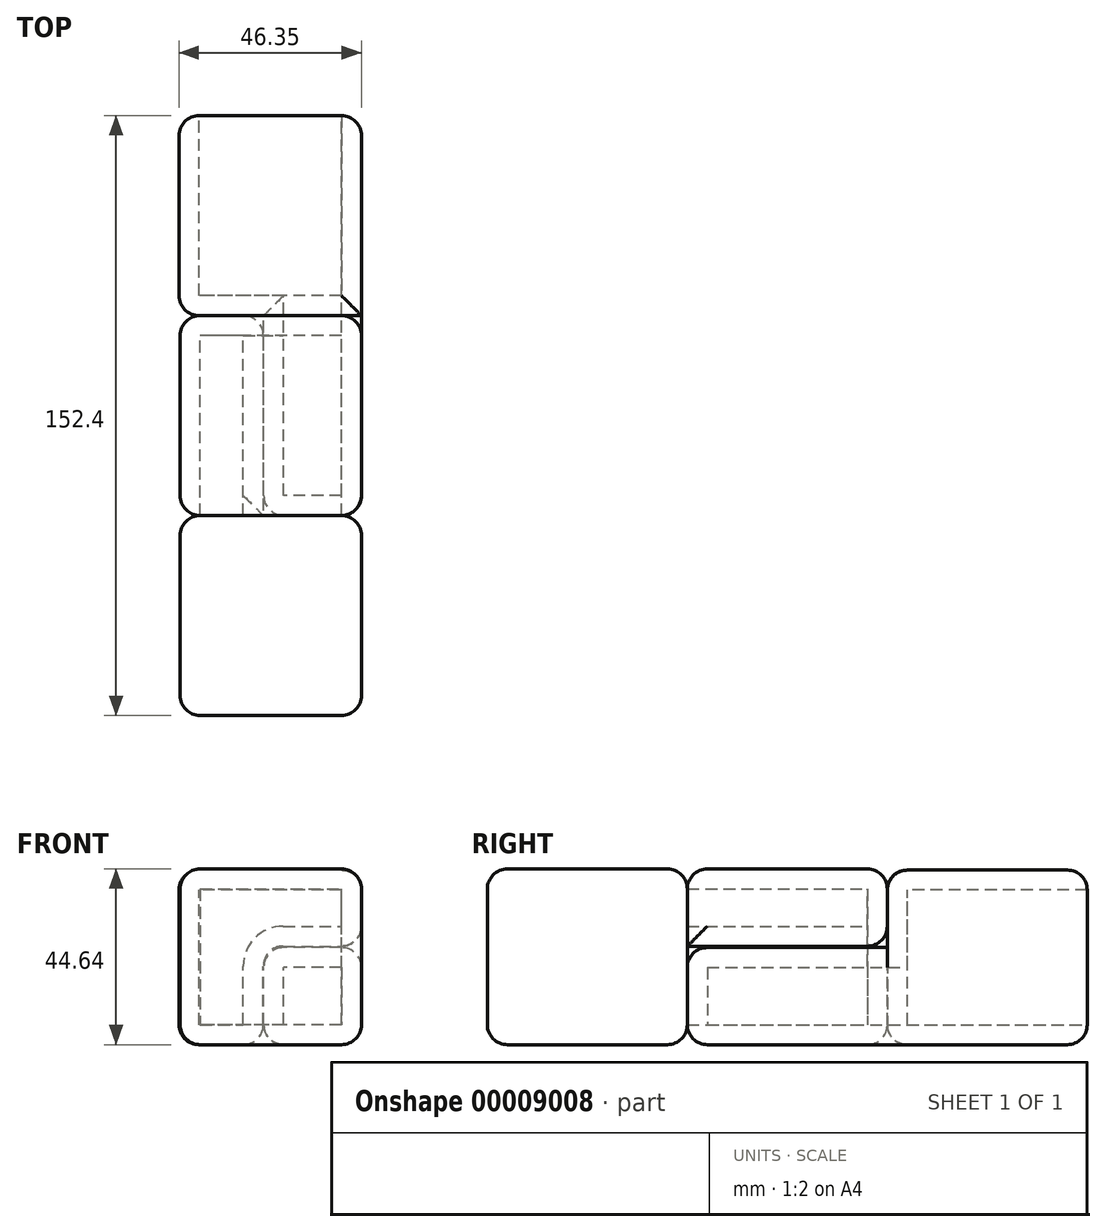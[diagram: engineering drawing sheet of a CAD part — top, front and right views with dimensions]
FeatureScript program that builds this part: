
annotation { "Feature Type Name" : "Feature", "Feature Type Description" : "" }
export const myFeature = defineFeature(function(context is Context, id is Id, definition is map)
    precondition{}
    {
        {
            var Q0;
            Q0=qCreatedBy(makeId("Front.planeOp"),FACE);
            var sketch = newSketch(context, id + "F0", { "sketchPlane" : qUnion([Q0])});
            skLineSegment(sketch, "E0.bottom", {"start": v(0, 0) * mm, "end": v(-46.35, 0) * mm});
            skLineSegment(sketch, "E0.top", {"start": v(0, 44.35) * mm, "end": v(-46.35, 44.35) * mm});
            skLineSegment(sketch, "E0.left", {"start": v(0, 0) * mm, "end": v(0, 44.35) * mm});
            skLineSegment(sketch, "E0.right", {"start": v(-46.35, 0) * mm, "end": v(-46.35, 44.35) * mm});
            skSolve(sketch);
        }
        {
            var Q0;
            Q0=makeQuery(id+"F0.imprint","IMPRINT",FACE,{"disambiguationData":[TD([[makeQuery(id+"F0.imprint","IMPRINT",EDGE,{"derivedFrom":sQuery(id+"F0.wireOp",EDGE,"E0.bottom")}),-1.0]])]});
            extrude(context, id + "F1", {"entities" : qUnion([Q0]), "depth" : 50.8 * mm});
        }
        {
            var Q0;
            Q0=makeQuery(id+"F1.opExtrude","CAP_FACE",FACE,{"disambiguationData":[OSD([sQuery(id+"F0.wireOp",EDGE,"E0.bottom"),sQuery(id+"F0.wireOp",EDGE,"E0.top"),sQuery(id+"F0.wireOp",EDGE,"E0.left"),sQuery(id+"F0.wireOp",EDGE,"E0.right")])],"isStart":false});
            var sketch = newSketch(context, id + "F2", { "sketchPlane" : qUnion([Q0])});
            skLineSegment(sketch, "E1.bottom", {"start": v(0, 0) * mm, "end": v(-24.82, 0) * mm});
            skLineSegment(sketch, "E1.top", {"start": v(0, 24.67) * mm, "end": v(-24.82, 24.67) * mm});
            skLineSegment(sketch, "E1.left", {"start": v(0, 0) * mm, "end": v(0, 24.67) * mm});
            skLineSegment(sketch, "E1.right", {"start": v(-24.82, 0) * mm, "end": v(-24.82, 24.67) * mm});
            skSolve(sketch);
        }
        {
            var Q0;
            Q0=makeQuery(id+"F2.imprint","IMPRINT",FACE,{"disambiguationData":[TD([[makeQuery(id+"F2.imprint","IMPRINT",EDGE,{"derivedFrom":sQuery(id+"F2.wireOp",EDGE,"E1.bottom")}),-1.0]])]});
            extrude(context, id + "F3", {"entities" : qUnion([Q0]), "operationType" : NewBodyOperationType.ADD, "depth" : 50.8 * mm});
        }
        {
            var Q0;
            Q0=makeQuery(id+"F1.opExtrude","CAP_EDGE",EDGE,{"disambiguationData":[OSD([sQuery(id+"F0.wireOp",EDGE,"E0.top")])],"isStart":false});
            var Q1;
            Q1=makeQuery(id+"F1.opExtrude","SWEPT_EDGE",EDGE,{"disambiguationData":[OSD([sQuery(id+"F0.wireOp",EDGE,"E0.top"),sQuery(id+"F0.wireOp",EDGE,"E0.left")])]});
            var Q2;
            Q2=makeQuery(id+"F1.opExtrude","SWEPT_EDGE",EDGE,{"disambiguationData":[OSD([sQuery(id+"F0.wireOp",EDGE,"E0.top"),sQuery(id+"F0.wireOp",EDGE,"E0.right")])]});
            var Q3;
            Q3=makeQuery(id+"F3.opExtrude","CAP_EDGE",EDGE,{"disambiguationData":[OSD([sQuery(id+"F2.wireOp",EDGE,"E1.top")])],"isStart":true});
            var Q4;
            Q4=makeQuery(id+"F3.opExtrude","SWEPT_EDGE",EDGE,{"disambiguationData":[OSD([sQuery(id+"F0.wireOp",EDGE,"E0.left"),sQuery(id+"F2.wireOp",EDGE,"E1.top"),sQuery(id+"F2.wireOp",EDGE,"E1.left")])]});
            var Q5;
            Q5=makeQuery(id+"F3.opExtrude","SWEPT_EDGE",EDGE,{"disambiguationData":[OSD([sQuery(id+"F2.wireOp",EDGE,"E1.top"),sQuery(id+"F2.wireOp",EDGE,"E1.right")])]});
            var Q6;
            Q6=makeQuery(id+"F3.opExtrude","CAP_EDGE",EDGE,{"disambiguationData":[OSD([sQuery(id+"F2.wireOp",EDGE,"E1.bottom")])],"isStart":false});
            var Q7;
            Q7=makeQuery(id+"F3.opExtrude","CAP_EDGE",EDGE,{"disambiguationData":[OSD([sQuery(id+"F2.wireOp",EDGE,"E1.right")])],"isStart":false});
            var Q8;
            Q8=makeQuery(id+"F3.opExtrude","CAP_EDGE",EDGE,{"disambiguationData":[OSD([sQuery(id+"F2.wireOp",EDGE,"E1.left")])],"isStart":false});
            var Q9;
            Q9=makeQuery(id+"F3.boolean.opBoolean","MERGE",EDGE,{"derivedFrom":[makeQuery(id+"F1.opExtrude","SWEPT_EDGE",EDGE,{"disambiguationData":[OSD([sQuery(id+"F0.wireOp",EDGE,"E0.bottom"),sQuery(id+"F0.wireOp",EDGE,"E0.left")])]}),makeQuery(id+"F3.opExtrude","SWEPT_EDGE",EDGE,{"disambiguationData":[OSD([sQuery(id+"F2.wireOp",EDGE,"E1.bottom"),sQuery(id+"F2.wireOp",EDGE,"E1.left")])]})]});
            var Q10;
            Q10=makeQuery(id+"F3.opExtrude","SWEPT_EDGE",EDGE,{"disambiguationData":[OSD([sQuery(id+"F0.wireOp",EDGE,"E0.bottom"),sQuery(id+"F2.wireOp",EDGE,"E1.bottom"),sQuery(id+"F2.wireOp",EDGE,"E1.right")])]});
            var Q11;
            Q11=makeQuery(id+"F1.opExtrude","CAP_EDGE",EDGE,{"disambiguationData":[OSD([sQuery(id+"F0.wireOp",EDGE,"E0.bottom")])],"isStart":false});
            var Q12;
            Q12=makeQuery(id+"F1.opExtrude","CAP_EDGE",EDGE,{"disambiguationData":[OSD([sQuery(id+"F0.wireOp",EDGE,"E0.right")])],"isStart":false});
            var Q13;
            Q13=makeQuery(id+"F1.opExtrude","SWEPT_EDGE",EDGE,{"disambiguationData":[OSD([sQuery(id+"F0.wireOp",EDGE,"E0.bottom"),sQuery(id+"F0.wireOp",EDGE,"E0.right")])]});
            var Q14;
            Q14=makeQuery(id+"F1.opExtrude","CAP_EDGE",EDGE,{"disambiguationData":[OSD([sQuery(id+"F0.wireOp",EDGE,"E0.bottom")])],"isStart":true});
            var Q15;
            Q15=makeQuery(id+"F1.opExtrude","CAP_EDGE",EDGE,{"disambiguationData":[OSD([sQuery(id+"F0.wireOp",EDGE,"E0.left")])],"isStart":true});
            var Q16;
            Q16=makeQuery(id+"F1.opExtrude","CAP_EDGE",EDGE,{"disambiguationData":[OSD([sQuery(id+"F0.wireOp",EDGE,"E0.right")])],"isStart":true});
            var Q17;
            Q17=makeQuery(id+"F1.opExtrude","CAP_EDGE",EDGE,{"disambiguationData":[OSD([sQuery(id+"F0.wireOp",EDGE,"E0.top")])],"isStart":true});
            var Q18;
            Q18=makeQuery(id+"F3.opExtrude","CAP_EDGE",EDGE,{"disambiguationData":[OSD([sQuery(id+"F2.wireOp",EDGE,"E1.top")])],"isStart":false});
            fillet(context, id + "F4", {"entities" : qUnion([Q0, Q1, Q2, Q3, Q4, Q5, Q6, Q7, Q8, Q9, Q10, Q11, Q12, Q13, Q14, Q15, Q16, Q17, Q18]), "radius" : 5.08 * mm, "tangentPropagation" : true, "allowEdgeOverflow" : false});
        }
        {
            var Q0;
            Q0=makeQuery(id+"F1.opExtrude","CAP_FACE",FACE,{"disambiguationData":[OSD([sQuery(id+"F0.wireOp",EDGE,"E0.bottom"),sQuery(id+"F0.wireOp",EDGE,"E0.top"),sQuery(id+"F0.wireOp",EDGE,"E0.left"),sQuery(id+"F0.wireOp",EDGE,"E0.right")])],"isStart":true});
            shell(context, id + "F5", {"entities" : qUnion([Q0]), "thickness" : 5.08 * mm});
        }
        {
            var Q0;
            Q0=qCreatedBy(makeId("Front.planeOp"),FACE);
            cPlane(context, id + "F6", {"entities" : qUnion([Q0]), "cplaneType" : CPlaneType.OFFSET, "offset" : 152.4 * mm, "width" : 152.4 * mm, "height" : 152.4 * mm});
        }
        {
            var Q0;
            Q0=qCreatedBy(id+"F6.planeOp",FACE);
            var sketch = newSketch(context, id + "F7", { "sketchPlane" : qUnion([Q0])});
            skLineSegment(sketch, "E2.bottom", {"start": v(-46.07, 44.64) * mm, "end": v(0, 44.64) * mm});
            skLineSegment(sketch, "E2.top", {"start": v(-46.07, 0) * mm, "end": v(0, 0) * mm});
            skLineSegment(sketch, "E2.left", {"start": v(-46.07, 44.64) * mm, "end": v(-46.07, 0) * mm});
            skLineSegment(sketch, "E2.right", {"start": v(0, 44.64) * mm, "end": v(0, 0) * mm});
            skSolve(sketch);
        }
        {
            var Q0;
            Q0=makeQuery(id+"F7.imprint","IMPRINT",FACE,{"disambiguationData":[TD([[makeQuery(id+"F7.imprint","IMPRINT",EDGE,{"derivedFrom":sQuery(id+"F7.wireOp",EDGE,"E2.bottom")}),-1.0]])]});
            extrude(context, id + "F8", {"entities" : qUnion([Q0]), "oppositeDirection" : true, "depth" : 50.8 * mm});
        }
        {
            var Q0;
            Q0=makeQuery(id+"F8.opExtrude","CAP_FACE",FACE,{"disambiguationData":[OSD([sQuery(id+"F7.wireOp",EDGE,"E2.bottom"),sQuery(id+"F7.wireOp",EDGE,"E2.top"),sQuery(id+"F7.wireOp",EDGE,"E2.left"),sQuery(id+"F7.wireOp",EDGE,"E2.right")])],"isStart":false});
            var sketch = newSketch(context, id + "F9", { "sketchPlane" : qUnion([Q0])});
            skLineSegment(sketch, "E3", {"start": v(0, 44.64) * mm, "end": v(46.07, 44.64) * mm});
            skLineSegment(sketch, "E4", {"start": v(46.07, 44.64) * mm, "end": v(46.07, 0) * mm});
            skLineSegment(sketch, "E5", {"start": v(46.07, 0) * mm, "end": v(25.34, 0) * mm});
            skLineSegment(sketch, "E6", {"start": v(25.34, 0) * mm, "end": v(25.34, 24.3) * mm});
            skLineSegment(sketch, "E7", {"start": v(25.34, 24.3) * mm, "end": v(0, 24.3) * mm});
            skLineSegment(sketch, "E8", {"start": v(0, 24.3) * mm, "end": v(0, 44.64) * mm});
            skSolve(sketch);
        }
        {
            var Q0;
            Q0=makeQuery(id+"F9.imprint","IMPRINT",FACE,{"disambiguationData":[TD([[makeQuery(id+"F9.imprint","IMPRINT",EDGE,{"derivedFrom":sQuery(id+"F9.wireOp",EDGE,"E3")}),1.0]])]});
            extrude(context, id + "F10", {"entities" : qUnion([Q0]), "depth" : 50.8 * mm});
        }
        {
            var Q0;
            Q0=makeQuery(id+"F10.opExtrude","SWEPT_BODY",BODY,{"disambiguationData":[OSD([sQuery(id+"F9.wireOp",EDGE,"E3"),sQuery(id+"F9.wireOp",EDGE,"E4"),sQuery(id+"F9.wireOp",EDGE,"E5"),sQuery(id+"F9.wireOp",EDGE,"E6"),sQuery(id+"F9.wireOp",EDGE,"E7"),sQuery(id+"F9.wireOp",EDGE,"E8")])]});
            deleteBodies(context, id + "F11", {"entities" : qUnion([Q0])});
        }
        {
            var Q0;
            Q0=makeQuery(id+"F8.opExtrude","CAP_FACE",FACE,{"disambiguationData":[OSD([sQuery(id+"F7.wireOp",EDGE,"E2.bottom"),sQuery(id+"F7.wireOp",EDGE,"E2.top"),sQuery(id+"F7.wireOp",EDGE,"E2.left"),sQuery(id+"F7.wireOp",EDGE,"E2.right")])],"isStart":false});
            var sketch = newSketch(context, id + "F12", { "sketchPlane" : qUnion([Q0])});
            skLineSegment(sketch, "E9", {"start": v(0, 44.64) * mm, "end": v(46.07, 44.64) * mm});
            skLineSegment(sketch, "E10", {"start": v(46.07, 44.64) * mm, "end": v(46.07, 0) * mm});
            skLineSegment(sketch, "E11", {"start": v(46.07, 0) * mm, "end": v(23.03, 0) * mm});
            skLineSegment(sketch, "E12", {"start": v(23.03, 0) * mm, "end": v(23.03, 25.02) * mm});
            skLineSegment(sketch, "E13", {"start": v(23.03, 25.02) * mm, "end": v(0, 25.02) * mm});
            skLineSegment(sketch, "E14", {"start": v(0, 25.02) * mm, "end": v(0, 44.64) * mm});
            skLineSegment(sketch, "E15.0", {"start": v(24.94, 0) * mm, "end": v(24.94, 25.02) * mm});
            skLineSegment(sketch, "E16", {"start": v(24.94, 25.02) * mm, "end": v(23.03, 25.02) * mm});
            skSolve(sketch);
        }
        {
            var Q0;
            Q0=makeQuery(id+"F12.imprint","IMPRINT",FACE,{"disambiguationData":[TD([[makeQuery(id+"F12.imprint","IMPRINT",EDGE,{"derivedFrom":sQuery(id+"F12.wireOp",EDGE,"E9")}),1.0]])]});
            extrude(context, id + "F13", {"entities" : qUnion([Q0]), "depth" : 50.8 * mm});
        }
        {
            var Q0;
            Q0=makeQuery(id+"F13.opExtrude","SWEPT_EDGE",EDGE,{"disambiguationData":[OSD([sQuery(id+"F12.wireOp",EDGE,"E9"),sQuery(id+"F12.wireOp",EDGE,"E14")])]});
            var Q1;
            Q1=makeQuery(id+"F13.opExtrude","SWEPT_EDGE",EDGE,{"disambiguationData":[OSD([sQuery(id+"F7.wireOp",EDGE,"E2.right"),sQuery(id+"F12.wireOp",EDGE,"E13"),sQuery(id+"F12.wireOp",EDGE,"E14")])]});
            var Q2;
            Q2=makeQuery(id+"F13.opExtrude","CAP_EDGE",EDGE,{"disambiguationData":[OSD([sQuery(id+"F12.wireOp",EDGE,"E14")])],"isStart":false});
            var Q3;
            Q3=makeQuery(id+"F13.opExtrude","SWEPT_EDGE",EDGE,{"disambiguationData":[OSD([sQuery(id+"F7.wireOp",EDGE,"E2.top"),sQuery(id+"F12.wireOp",EDGE,"E11"),sQuery(id+"F12.wireOp",EDGE,"E12")])]});
            var Q4;
            Q4=makeQuery(id+"F13.opExtrude","CAP_EDGE",EDGE,{"disambiguationData":[OSD([sQuery(id+"F12.wireOp",EDGE,"E11")])],"isStart":false});
            var Q5;
            Q5=makeQuery(id+"F13.opExtrude","SWEPT_EDGE",EDGE,{"disambiguationData":[OSD([sQuery(id+"F12.wireOp",EDGE,"E10"),sQuery(id+"F12.wireOp",EDGE,"E11")])]});
            var Q6;
            Q6=makeQuery(id+"F8.opExtrude","SWEPT_EDGE",EDGE,{"disambiguationData":[OSD([sQuery(id+"F7.wireOp",EDGE,"E2.bottom"),sQuery(id+"F7.wireOp",EDGE,"E2.right")])]});
            var Q7;
            Q7=makeQuery(id+"F8.opExtrude","CAP_EDGE",EDGE,{"disambiguationData":[OSD([sQuery(id+"F7.wireOp",EDGE,"E2.right")])],"isStart":true});
            var Q8;
            Q8=makeQuery(id+"F8.opExtrude","SWEPT_EDGE",EDGE,{"disambiguationData":[OSD([sQuery(id+"F7.wireOp",EDGE,"E2.top"),sQuery(id+"F7.wireOp",EDGE,"E2.right")])]});
            var Q9;
            Q9=makeQuery(id+"F8.opExtrude","CAP_EDGE",EDGE,{"disambiguationData":[OSD([sQuery(id+"F7.wireOp",EDGE,"E2.right")])],"isStart":false});
            var Q10;
            Q10=makeQuery(id+"F8.opExtrude","CAP_EDGE",EDGE,{"disambiguationData":[OSD([sQuery(id+"F7.wireOp",EDGE,"E2.top")])],"isStart":false});
            var Q11;
            Q11=makeQuery(id+"F8.opExtrude","SWEPT_EDGE",EDGE,{"disambiguationData":[OSD([sQuery(id+"F7.wireOp",EDGE,"E2.top"),sQuery(id+"F7.wireOp",EDGE,"E2.left")])]});
            var Q12;
            Q12=makeQuery(id+"F8.opExtrude","CAP_EDGE",EDGE,{"disambiguationData":[OSD([sQuery(id+"F7.wireOp",EDGE,"E2.top")])],"isStart":true});
            var Q13;
            Q13=makeQuery(id+"F8.opExtrude","CAP_EDGE",EDGE,{"disambiguationData":[OSD([sQuery(id+"F7.wireOp",EDGE,"E2.bottom")])],"isStart":true});
            var Q14;
            Q14=makeQuery(id+"F8.opExtrude","CAP_EDGE",EDGE,{"disambiguationData":[OSD([sQuery(id+"F7.wireOp",EDGE,"E2.left")])],"isStart":true});
            var Q15;
            Q15=makeQuery(id+"F8.opExtrude","SWEPT_EDGE",EDGE,{"disambiguationData":[OSD([sQuery(id+"F7.wireOp",EDGE,"E2.bottom"),sQuery(id+"F7.wireOp",EDGE,"E2.left")])]});
            var Q16;
            Q16=makeQuery(id+"F13.opExtrude","SWEPT_EDGE",EDGE,{"disambiguationData":[OSD([sQuery(id+"F12.wireOp",EDGE,"E9"),sQuery(id+"F12.wireOp",EDGE,"E10")])]});
            var Q17;
            Q17=makeQuery(id+"F13.opExtrude","SWEPT_FACE",FACE,{"disambiguationData":[OSD([sQuery(id+"F12.wireOp",EDGE,"E9")])]});
            var Q18;
            Q18=makeQuery(id+"F13.opExtrude","CAP_EDGE",EDGE,{"disambiguationData":[OSD([sQuery(id+"F12.wireOp",EDGE,"E13"),sQuery(id+"F12.wireOp",EDGE,"E16")])],"isStart":false});
            var Q19;
            Q19=makeQuery(id+"F13.opExtrude","CAP_EDGE",EDGE,{"disambiguationData":[OSD([sQuery(id+"F12.wireOp",EDGE,"E15.0")])],"isStart":false});
            var Q20;
            Q20=makeQuery(id+"F13.opExtrude","CAP_EDGE",EDGE,{"disambiguationData":[OSD([sQuery(id+"F12.wireOp",EDGE,"E10")])],"isStart":false});
            var Q21;
            Q21=makeQuery(id+"F13.opExtrude","SWEPT_EDGE",EDGE,{"disambiguationData":[OSD([sQuery(id+"F12.wireOp",EDGE,"E15.0"),sQuery(id+"F12.wireOp",EDGE,"E16")])]});
            var Q22;
            Q22=makeQuery(id+"F8.opExtrude","CAP_EDGE",EDGE,{"disambiguationData":[OSD([sQuery(id+"F7.wireOp",EDGE,"E2.bottom")])],"isStart":false});
            var Q23;
            Q23=makeQuery(id+"F13.opExtrude","SWEPT_FACE",FACE,{"disambiguationData":[OSD([sQuery(id+"F12.wireOp",EDGE,"E10")])]});
            var Q24;
            Q24=makeQuery(id+"F8.opExtrude","CAP_EDGE",EDGE,{"disambiguationData":[OSD([sQuery(id+"F7.wireOp",EDGE,"E2.left")])],"isStart":false});
            var Q25;
            Q25=makeQuery(id+"F13.opExtrude","SWEPT_FACE",FACE,{"disambiguationData":[OSD([sQuery(id+"F12.wireOp",EDGE,"E11")])]});
            var Q26;
            Q26=makeQuery(id+"F13.opExtrude","CAP_EDGE",EDGE,{"disambiguationData":[OSD([sQuery(id+"F12.wireOp",EDGE,"E14")])],"isStart":true});
            fillet(context, id + "F14", {"entities" : qUnion([Q0, Q1, Q2, Q3, Q4, Q5, Q6, Q7, Q8, Q9, Q10, Q11, Q12, Q13, Q14, Q15, Q16, Q17, Q18, Q19, Q20, Q21, Q22, Q23, Q24, Q25, Q26]), "radius" : 5.08 * mm, "tangentPropagation" : true, "allowEdgeOverflow" : false});
        }
        {
            var Q0;
            Q0=makeQuery(id+"F13.opExtrude","CAP_FACE",FACE,{"disambiguationData":[OSD([sQuery(id+"F12.wireOp",EDGE,"E9"),sQuery(id+"F12.wireOp",EDGE,"E10"),sQuery(id+"F12.wireOp",EDGE,"E11"),sQuery(id+"F12.wireOp",EDGE,"E13"),sQuery(id+"F12.wireOp",EDGE,"E14"),sQuery(id+"F12.wireOp",EDGE,"E15.0"),sQuery(id+"F12.wireOp",EDGE,"E16")])],"isStart":true});
            shell(context, id + "F15", {"entities" : qUnion([Q0]), "thickness" : 5.08 * mm});
        }
    });
